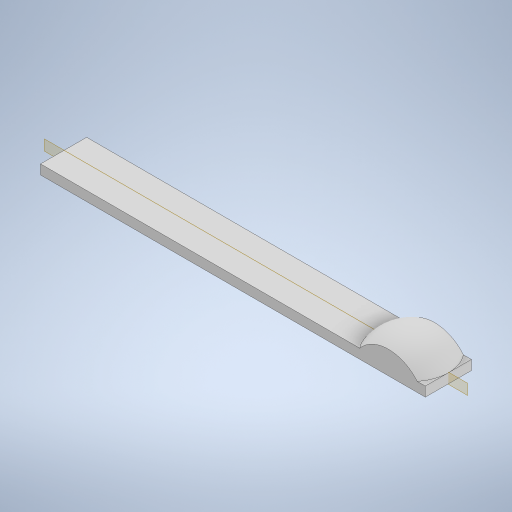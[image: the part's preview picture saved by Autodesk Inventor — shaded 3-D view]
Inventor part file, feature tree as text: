
AUTODESK INVENTOR PART (.ipt)
format: ipt  version: 2024.2 (Build 282272000, 272)  size: 261,120 bytes
history: native  units: in
note: dims shown in document units (in); Inventor stores cm internally (conversion verified against a paired STEP export)
features: sketch x3, extrude x2, plane x1, revolve x1
ambient origin geometry x8: Origin, YZ Plane, XZ Plane, XY Plane, X Axis, Y Axis, Z Axis, Center Point
bodies: Solid1 (feature_tree)
feature tree (7):
  extrude  "Extrusion1"  Depth=2.5in
  plane  "Work Plane1"
  revolve  "Revolution1"  [1 undecoded]
  extrude  "Extrusion2"  TaperAngle=0.0deg  [1 undecoded]
  sketch  "Sketch1"  dims[d0=0.3in d1=2.5in]
  sketch  "Sketch2"  dims[d2=0.0625in d3=0.0in d4=-0.15in]
  sketch  "Sketch3"  dims[d5=360.0deg d7=0.0in d8=0.0in]
note: 2 required parameter values undecoded (feature->parameter linkage not recoverable at this tier; creation-order binding heuristic only, values carry confidence <= 0.55)